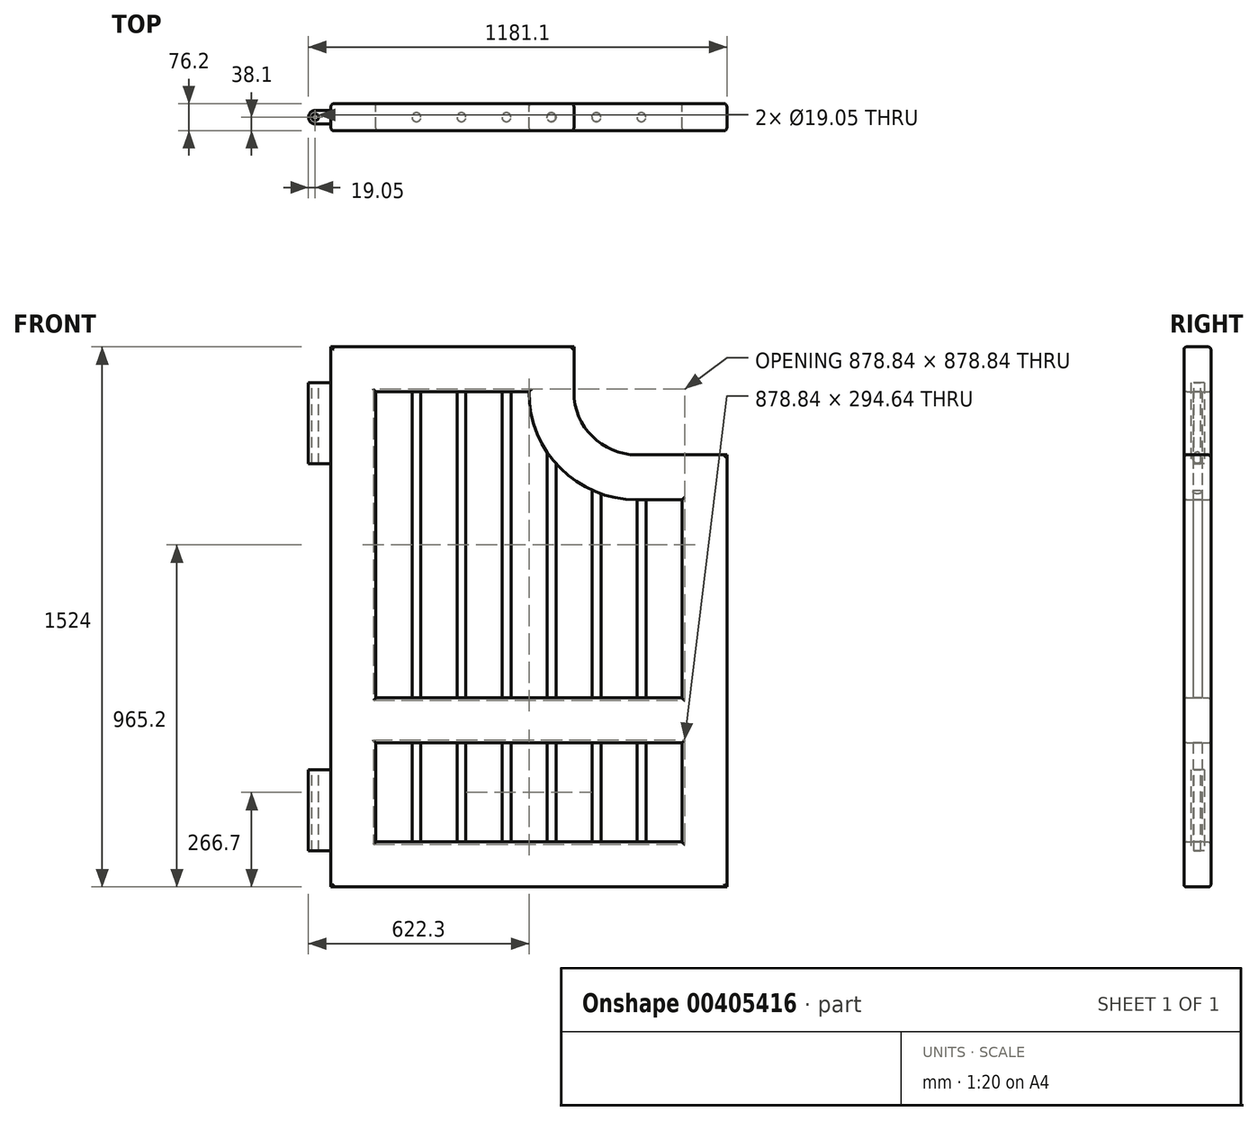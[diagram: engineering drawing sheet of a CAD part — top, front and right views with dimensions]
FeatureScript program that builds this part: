
annotation { "Feature Type Name" : "Feature", "Feature Type Description" : "" }
export const myFeature = defineFeature(function(context is Context, id is Id, definition is map)
    precondition{}
    {
        {
            var Q0;
            Q0=qCreatedBy(makeId("Front.planeOp"),FACE);
            var sketch = newSketch(context, id + "F0", { "sketchPlane" : qUnion([Q0])});
            skLineSegment(sketch, "E0", {"start": v(-558.8, -609.6) * mm, "end": v(558.8, -609.6) * mm});
            skLineSegment(sketch, "E1", {"start": v(558.8, -609.6) * mm, "end": v(558.8, 609.6) * mm});
            skLineSegment(sketch, "E2", {"start": v(558.8, 609.6) * mm, "end": v(304.8, 609.6) * mm});
            skLineSegment(sketch, "E3", {"start": v(-558.8, -609.6) * mm, "end": v(-558.8, 914.4) * mm});
            skLineSegment(sketch, "E4", {"start": v(-558.8, 914.4) * mm, "end": v(127, 914.4) * mm});
            skLineSegment(sketch, "E5.bottom", {"start": v(-431.8, -203.2) * mm, "end": v(431.8, -203.2) * mm});
            skLineSegment(sketch, "E5.top", {"start": v(-431.8, -482.6) * mm, "end": v(431.8, -482.6) * mm});
            skLineSegment(sketch, "E5.left", {"start": v(-431.8, -203.2) * mm, "end": v(-431.8, -482.6) * mm});
            skLineSegment(sketch, "E5.right", {"start": v(431.8, -203.2) * mm, "end": v(431.8, -482.6) * mm});
            skLineSegment(sketch, "E6", {"start": v(0, 787.4) * mm, "end": v(-431.8, 787.4) * mm});
            skLineSegment(sketch, "E7", {"start": v(-431.8, 787.4) * mm, "end": v(-431.8, -76.2) * mm});
            skLineSegment(sketch, "E8", {"start": v(431.8, -76.2) * mm, "end": v(431.8, 482.6) * mm});
            skLineSegment(sketch, "E9", {"start": v(431.8, 482.6) * mm, "end": v(304.8, 482.6) * mm});
            skArc(sketch, "E10", {"start": v(304.8, 482.6) * mm, "mid": v(89.27, 571.87) * mm, "end": v(0, 787.4) * mm});
            skLineSegment(sketch, "E11", {"start": v(-431.8, -76.2) * mm, "end": v(431.8, -76.2) * mm});
            skLineSegment(sketch, "E12", {"start": v(127, 914.4) * mm, "end": v(127, 787.4) * mm});
            skArc(sketch, "E13", {"start": v(304.8, 609.6) * mm, "mid": v(179.08, 661.68) * mm, "end": v(127, 787.4) * mm});
            skSolve(sketch);
        }
        {
            var Q0;
            Q0=makeQuery(id+"F0.imprint","IMPRINT",FACE,{"disambiguationData":[TD([[makeQuery(id+"F0.imprint","IMPRINT",EDGE,{"derivedFrom":sQuery(id+"F0.wireOp",EDGE,"E0")}),1.0]])]});
            extrude(context, id + "F1", {"entities" : qUnion([Q0]), "depth" : 76.2 * mm, "symmetric" : true});
        }
        {
            var Q0;
            Q0=makeQuery(id+"F1.opExtrude","CAP_FACE",FACE,{"disambiguationData":[OSD([sQuery(id+"F0.wireOp",EDGE,"E0"),sQuery(id+"F0.wireOp",EDGE,"E1"),sQuery(id+"F0.wireOp",EDGE,"E2"),sQuery(id+"F0.wireOp",EDGE,"E3"),sQuery(id+"F0.wireOp",EDGE,"E4"),sQuery(id+"F0.wireOp",EDGE,"45394d91-6a49-4310-a277-840086c14d09"),sQuery(id+"F0.wireOp",EDGE,"E5.bottom"),sQuery(id+"F0.wireOp",EDGE,"E5.top"),sQuery(id+"F0.wireOp",EDGE,"E5.left"),sQuery(id+"F0.wireOp",EDGE,"E5.right"),sQuery(id+"F0.wireOp",EDGE,"E6"),sQuery(id+"F0.wireOp",EDGE,"E7"),sQuery(id+"F0.wireOp",EDGE,"E8"),sQuery(id+"F0.wireOp",EDGE,"E9"),sQuery(id+"F0.wireOp",EDGE,"E10"),sQuery(id+"F0.wireOp",EDGE,"E11")])],"isStart":true});
            var Q1;
            Q1=makeQuery(id+"F1.opExtrude","CAP_FACE",FACE,{"disambiguationData":[OSD([sQuery(id+"F0.wireOp",EDGE,"E0"),sQuery(id+"F0.wireOp",EDGE,"E1"),sQuery(id+"F0.wireOp",EDGE,"E2"),sQuery(id+"F0.wireOp",EDGE,"E3"),sQuery(id+"F0.wireOp",EDGE,"E4"),sQuery(id+"F0.wireOp",EDGE,"45394d91-6a49-4310-a277-840086c14d09"),sQuery(id+"F0.wireOp",EDGE,"E5.bottom"),sQuery(id+"F0.wireOp",EDGE,"E5.top"),sQuery(id+"F0.wireOp",EDGE,"E5.left"),sQuery(id+"F0.wireOp",EDGE,"E5.right"),sQuery(id+"F0.wireOp",EDGE,"E6"),sQuery(id+"F0.wireOp",EDGE,"E7"),sQuery(id+"F0.wireOp",EDGE,"E8"),sQuery(id+"F0.wireOp",EDGE,"E9"),sQuery(id+"F0.wireOp",EDGE,"E10"),sQuery(id+"F0.wireOp",EDGE,"E11")])],"isStart":false});
            fillet(context, id + "F2", {"entities" : qUnion([Q0, Q1]), "radius" : 7.62 * mm, "tangentPropagation" : true, "allowEdgeOverflow" : false});
        }
        {
            var Q0;
            Q0=makeQuery(id+"F1.opExtrude","SWEPT_FACE",FACE,{"disambiguationData":[OSD([sQuery(id+"F0.wireOp",EDGE,"E5.top")])]});
            var sketch = newSketch(context, id + "F3", { "sketchPlane" : qUnion([Q0])});
            skLineSegment(sketch, "E14", {"start": v(-431.8, 0) * mm, "end": v(431.8, 0) * mm, "construction": true});
            skCircle(sketch, "E15", {"center": v(-317.5, 0) * mm, "radius": 12.7 * mm});
            skCircle(sketch, "E16.1.0.0", {"center": v(-190.5, 0) * mm, "radius": 12.7 * mm});
            skCircle(sketch, "E16.2.0.0", {"center": v(-63.5, 0) * mm, "radius": 12.7 * mm});
            skCircle(sketch, "E16.3.0.0", {"center": v(63.5, 0) * mm, "radius": 12.7 * mm});
            skCircle(sketch, "E16.4.0.0", {"center": v(190.5, 0) * mm, "radius": 12.7 * mm});
            skCircle(sketch, "E16.5.0.0", {"center": v(317.5, 0) * mm, "radius": 12.7 * mm});
            skLineSegment(sketch, "E16.direction1", {"start": v(-317.5, 0) * mm, "end": v(-190.5, 0) * mm, "construction": true});
            skSolve(sketch);
        }
        {
            var Q0;
            Q0=makeQuery(id+"F3.imprint","IMPRINT",FACE,{"disambiguationData":[TD([[makeQuery(id+"F3.imprint","IMPRINT",EDGE,{"derivedFrom":sQuery(id+"F3.wireOp",EDGE,"E16.24.0.0")}),1.0]])]});
            var Q1;
            Q1=makeQuery(id+"F3.imprint","IMPRINT",FACE,{"disambiguationData":[TD([[makeQuery(id+"F3.imprint","IMPRINT",EDGE,{"derivedFrom":sQuery(id+"F3.wireOp",EDGE,"E16.26.0.0")}),1.0]])]});
            var Q2;
            Q2=makeQuery(id+"F3.imprint","IMPRINT",FACE,{"disambiguationData":[TD([[makeQuery(id+"F3.imprint","IMPRINT",EDGE,{"derivedFrom":sQuery(id+"F3.wireOp",EDGE,"E16.25.0.0")}),1.0]])]});
            var Q3;
            Q3=makeQuery(id+"F3.imprint","IMPRINT",FACE,{"disambiguationData":[TD([[makeQuery(id+"F3.imprint","IMPRINT",EDGE,{"derivedFrom":sQuery(id+"F3.wireOp",EDGE,"E16.27.0.0")}),1.0]])]});
            var Q4;
            Q4=makeQuery(id+"F3.imprint","IMPRINT",FACE,{"disambiguationData":[TD([[makeQuery(id+"F3.imprint","IMPRINT",EDGE,{"derivedFrom":sQuery(id+"F3.wireOp",EDGE,"E16.23.0.0")}),1.0]])]});
            var Q5;
            Q5=makeQuery(id+"F3.imprint","IMPRINT",FACE,{"disambiguationData":[TD([[makeQuery(id+"F3.imprint","IMPRINT",EDGE,{"derivedFrom":sQuery(id+"F3.wireOp",EDGE,"E16.22.0.0")}),1.0]])]});
            var Q6;
            Q6=makeQuery(id+"F3.imprint","IMPRINT",FACE,{"disambiguationData":[TD([[makeQuery(id+"F3.imprint","IMPRINT",EDGE,{"derivedFrom":sQuery(id+"F3.wireOp",EDGE,"E16.2.0.0")}),1.0]])]});
            var Q7;
            Q7=makeQuery(id+"F3.imprint","IMPRINT",FACE,{"disambiguationData":[TD([[makeQuery(id+"F3.imprint","IMPRINT",EDGE,{"derivedFrom":sQuery(id+"F3.wireOp",EDGE,"E16.7.0.0")}),1.0]])]});
            var Q8;
            Q8=makeQuery(id+"F3.imprint","IMPRINT",FACE,{"disambiguationData":[TD([[makeQuery(id+"F3.imprint","IMPRINT",EDGE,{"derivedFrom":sQuery(id+"F3.wireOp",EDGE,"E16.9.0.0")}),1.0]])]});
            var Q9;
            Q9=makeQuery(id+"F3.imprint","IMPRINT",FACE,{"disambiguationData":[TD([[makeQuery(id+"F3.imprint","IMPRINT",EDGE,{"derivedFrom":sQuery(id+"F3.wireOp",EDGE,"E16.8.0.0")}),1.0]])]});
            var Q10;
            Q10=makeQuery(id+"F3.imprint","IMPRINT",FACE,{"disambiguationData":[TD([[makeQuery(id+"F3.imprint","IMPRINT",EDGE,{"derivedFrom":sQuery(id+"F3.wireOp",EDGE,"E16.3.0.0")}),1.0]])]});
            var Q11;
            Q11=makeQuery(id+"F3.imprint","IMPRINT",FACE,{"disambiguationData":[TD([[makeQuery(id+"F3.imprint","IMPRINT",EDGE,{"derivedFrom":sQuery(id+"F3.wireOp",EDGE,"E16.19.0.0")}),1.0]])]});
            var Q12;
            Q12=makeQuery(id+"F3.imprint","IMPRINT",FACE,{"disambiguationData":[TD([[makeQuery(id+"F3.imprint","IMPRINT",EDGE,{"derivedFrom":sQuery(id+"F3.wireOp",EDGE,"E16.12.0.0")}),1.0]])]});
            var Q13;
            Q13=makeQuery(id+"F3.imprint","IMPRINT",FACE,{"disambiguationData":[TD([[makeQuery(id+"F3.imprint","IMPRINT",EDGE,{"derivedFrom":sQuery(id+"F3.wireOp",EDGE,"E16.14.0.0")}),1.0]])]});
            var Q14;
            Q14=makeQuery(id+"F3.imprint","IMPRINT",FACE,{"disambiguationData":[TD([[makeQuery(id+"F3.imprint","IMPRINT",EDGE,{"derivedFrom":sQuery(id+"F3.wireOp",EDGE,"E16.21.0.0")}),1.0]])]});
            var Q15;
            Q15=makeQuery(id+"F3.imprint","IMPRINT",FACE,{"disambiguationData":[TD([[makeQuery(id+"F3.imprint","IMPRINT",EDGE,{"derivedFrom":sQuery(id+"F3.wireOp",EDGE,"E16.17.0.0")}),1.0]])]});
            var Q16;
            Q16=makeQuery(id+"F3.imprint","IMPRINT",FACE,{"disambiguationData":[TD([[makeQuery(id+"F3.imprint","IMPRINT",EDGE,{"derivedFrom":sQuery(id+"F3.wireOp",EDGE,"E16.16.0.0")}),1.0]])]});
            var Q17;
            Q17=makeQuery(id+"F3.imprint","IMPRINT",FACE,{"disambiguationData":[TD([[makeQuery(id+"F3.imprint","IMPRINT",EDGE,{"derivedFrom":sQuery(id+"F3.wireOp",EDGE,"E16.20.0.0")}),1.0]])]});
            var Q18;
            Q18=makeQuery(id+"F3.imprint","IMPRINT",FACE,{"disambiguationData":[TD([[makeQuery(id+"F3.imprint","IMPRINT",EDGE,{"derivedFrom":sQuery(id+"F3.wireOp",EDGE,"E16.18.0.0")}),1.0]])]});
            var Q19;
            Q19=makeQuery(id+"F3.imprint","IMPRINT",FACE,{"disambiguationData":[TD([[makeQuery(id+"F3.imprint","IMPRINT",EDGE,{"derivedFrom":sQuery(id+"F3.wireOp",EDGE,"E16.15.0.0")}),1.0]])]});
            var Q20;
            Q20=makeQuery(id+"F3.imprint","IMPRINT",FACE,{"disambiguationData":[TD([[makeQuery(id+"F3.imprint","IMPRINT",EDGE,{"derivedFrom":sQuery(id+"F3.wireOp",EDGE,"E16.6.0.0")}),1.0]])]});
            var Q21;
            Q21=makeQuery(id+"F3.imprint","IMPRINT",FACE,{"disambiguationData":[TD([[makeQuery(id+"F3.imprint","IMPRINT",EDGE,{"derivedFrom":sQuery(id+"F3.wireOp",EDGE,"E16.11.0.0")}),1.0]])]});
            var Q22;
            Q22=makeQuery(id+"F3.imprint","IMPRINT",FACE,{"disambiguationData":[TD([[makeQuery(id+"F3.imprint","IMPRINT",EDGE,{"derivedFrom":sQuery(id+"F3.wireOp",EDGE,"E16.10.0.0")}),1.0]])]});
            var Q23;
            Q23=makeQuery(id+"F3.imprint","IMPRINT",FACE,{"disambiguationData":[TD([[makeQuery(id+"F3.imprint","IMPRINT",EDGE,{"derivedFrom":sQuery(id+"F3.wireOp",EDGE,"E16.4.0.0")}),1.0]])]});
            var Q24;
            Q24=makeQuery(id+"F3.imprint","IMPRINT",FACE,{"disambiguationData":[TD([[makeQuery(id+"F3.imprint","IMPRINT",EDGE,{"derivedFrom":sQuery(id+"F3.wireOp",EDGE,"E16.13.0.0")}),1.0]])]});
            var Q25;
            Q25=makeQuery(id+"F3.imprint","IMPRINT",FACE,{"disambiguationData":[TD([[makeQuery(id+"F3.imprint","IMPRINT",EDGE,{"derivedFrom":sQuery(id+"F3.wireOp",EDGE,"E16.5.0.0")}),1.0]])]});
            var Q26;
            Q26=makeQuery(id+"F3.imprint","IMPRINT",FACE,{"disambiguationData":[TD([[makeQuery(id+"F3.imprint","IMPRINT",EDGE,{"derivedFrom":sQuery(id+"F3.wireOp",EDGE,"E16.1.0.0")}),1.0]])]});
            var Q27;
            Q27=makeQuery(id+"F3.imprint","IMPRINT",FACE,{"disambiguationData":[TD([[makeQuery(id+"F3.imprint","IMPRINT",EDGE,{"derivedFrom":sQuery(id+"F3.wireOp",EDGE,"E15")}),1.0]])]});
            extrude(context, id + "F4", {"entities" : qUnion([Q0, Q1, Q2, Q3, Q4, Q5, Q6, Q7, Q8, Q9, Q10, Q11, Q12, Q13, Q14, Q15, Q16, Q17, Q18, Q19, Q20, Q21, Q22, Q23, Q24, Q25, Q26, Q27]), "operationType" : NewBodyOperationType.ADD, "flatOperationType" : FlatOperationType.REMOVE, "offsetDistance" : 25.4 * mm, "depth" : 1071.88 * mm, "domain" : OperationDomain.MODEL});
        }
        {
            var Q0;
            Q0=makeQuery(id+"F4.opExtrude","CAP_FACE",FACE,{"disambiguationData":[OSD([sQuery(id+"F3.wireOp",EDGE,"E16.1.0.0")])],"isStart":false});
            var Q1;
            Q1=makeQuery(id+"F4.opExtrude","CAP_FACE",FACE,{"disambiguationData":[OSD([sQuery(id+"F3.wireOp",EDGE,"E15")])],"isStart":false});
            extrude(context, id + "F5", {"entities" : qUnion([Q0, Q1]), "operationType" : NewBodyOperationType.ADD, "flatOperationType" : FlatOperationType.REMOVE, "offsetDistance" : 25.4 * mm, "depth" : 289.56 * mm, "domain" : OperationDomain.MODEL});
        }
        {
            var Q0;
            Q0=makeQuery(id+"F1.opExtrude","SWEPT_FACE",FACE,{"disambiguationData":[OSD([sQuery(id+"F0.wireOp",EDGE,"E3")])]});
            var sketch = newSketch(context, id + "F6", { "sketchPlane" : qUnion([Q0])});
            skLineSegment(sketch, "E17.bottom", {"start": v(-19.05, -279.4) * mm, "end": v(19.05, -279.4) * mm});
            skLineSegment(sketch, "E17.top", {"start": v(-19.05, -508) * mm, "end": v(19.05, -508) * mm});
            skLineSegment(sketch, "E17.left", {"start": v(-19.05, -279.4) * mm, "end": v(-19.05, -508) * mm});
            skLineSegment(sketch, "E17.right", {"start": v(19.05, -279.4) * mm, "end": v(19.05, -508) * mm});
            skLineSegment(sketch, "E18.bottom", {"start": v(-19.05, 812.8) * mm, "end": v(19.05, 812.8) * mm});
            skLineSegment(sketch, "E18.top", {"start": v(-19.05, 584.2) * mm, "end": v(19.05, 584.2) * mm});
            skLineSegment(sketch, "E18.left", {"start": v(-19.05, 812.8) * mm, "end": v(-19.05, 584.2) * mm});
            skLineSegment(sketch, "E18.right", {"start": v(19.05, 812.8) * mm, "end": v(19.05, 584.2) * mm});
            skSolve(sketch);
        }
        {
            var Q0;
            Q0=makeQuery(id+"F6.imprint","IMPRINT",FACE,{"disambiguationData":[TD([[makeQuery(id+"F6.imprint","IMPRINT",EDGE,{"derivedFrom":sQuery(id+"F6.wireOp",EDGE,"E18.bottom")}),-1.0]])]});
            var Q1;
            Q1=makeQuery(id+"F6.imprint","IMPRINT",FACE,{"disambiguationData":[TD([[makeQuery(id+"F6.imprint","IMPRINT",EDGE,{"derivedFrom":sQuery(id+"F6.wireOp",EDGE,"E17.bottom")}),-1.0]])]});
            extrude(context, id + "F7", {"entities" : qUnion([Q0, Q1]), "operationType" : NewBodyOperationType.ADD, "depth" : 63.5 * mm});
        }
        {
            var Q0;
            Q0=makeQuery(id+"F7.opExtrude","CAP_EDGE",EDGE,{"disambiguationData":[OSD([sQuery(id+"F6.wireOp",EDGE,"E18.right")])],"isStart":false});
            var Q1;
            Q1=makeQuery(id+"F7.opExtrude","CAP_EDGE",EDGE,{"disambiguationData":[OSD([sQuery(id+"F6.wireOp",EDGE,"E18.left")])],"isStart":false});
            var Q2;
            Q2=makeQuery(id+"F7.opExtrude","CAP_EDGE",EDGE,{"disambiguationData":[OSD([sQuery(id+"F6.wireOp",EDGE,"E17.left")])],"isStart":false});
            var Q3;
            Q3=makeQuery(id+"F7.opExtrude","CAP_EDGE",EDGE,{"disambiguationData":[OSD([sQuery(id+"F6.wireOp",EDGE,"E17.right")])],"isStart":false});
            fillet(context, id + "F8", {"entities" : qUnion([Q0, Q1, Q2, Q3]), "radius" : 19.05 * mm, "tangentPropagation" : true, "allowEdgeOverflow" : false});
        }
        {
            var Q0;
            Q0=makeQuery(id+"F7.opExtrude","SWEPT_FACE",FACE,{"disambiguationData":[OSD([sQuery(id+"F6.wireOp",EDGE,"E18.bottom")])]});
            var sketch = newSketch(context, id + "F9", { "sketchPlane" : qUnion([Q0])});
            skCircle(sketch, "E19", {"center": v(-603.25, 0) * mm, "radius": 9.53 * mm});
            skSolve(sketch);
        }
        {
            var Q0;
            Q0=makeQuery(id+"F9.imprint","IMPRINT",FACE,{"disambiguationData":[TD([[makeQuery(id+"F9.imprint","IMPRINT",EDGE,{"derivedFrom":sQuery(id+"F9.wireOp",EDGE,"E19")}),1.0]])]});
            extrude(context, id + "F10", {"entities" : qUnion([Q0]), "operationType" : NewBodyOperationType.REMOVE, "endBound" : BoundingType.THROUGH_ALL, "oppositeDirection" : true, "depth" : 25.4 * mm});
        }
        {
            var Q0;
            Q0=makeQuery(id+"F4.opExtrude","CAP_FACE",FACE,{"disambiguationData":[OSD([sQuery(id+"F3.wireOp",EDGE,"E16.2.0.0")])],"isStart":false});
            extrude(context, id + "F11", {"entities" : qUnion([Q0]), "operationType" : NewBodyOperationType.ADD, "depth" : 264.16 * mm});
        }
        {
            var Q0;
            Q0=makeQuery(id+"F4.opExtrude","CAP_FACE",FACE,{"disambiguationData":[OSD([sQuery(id+"F3.wireOp",EDGE,"E16.3.0.0")])],"isStart":false});
            extrude(context, id + "F12", {"entities" : qUnion([Q0]), "operationType" : NewBodyOperationType.ADD, "depth" : 106.68 * mm});
        }
    });
